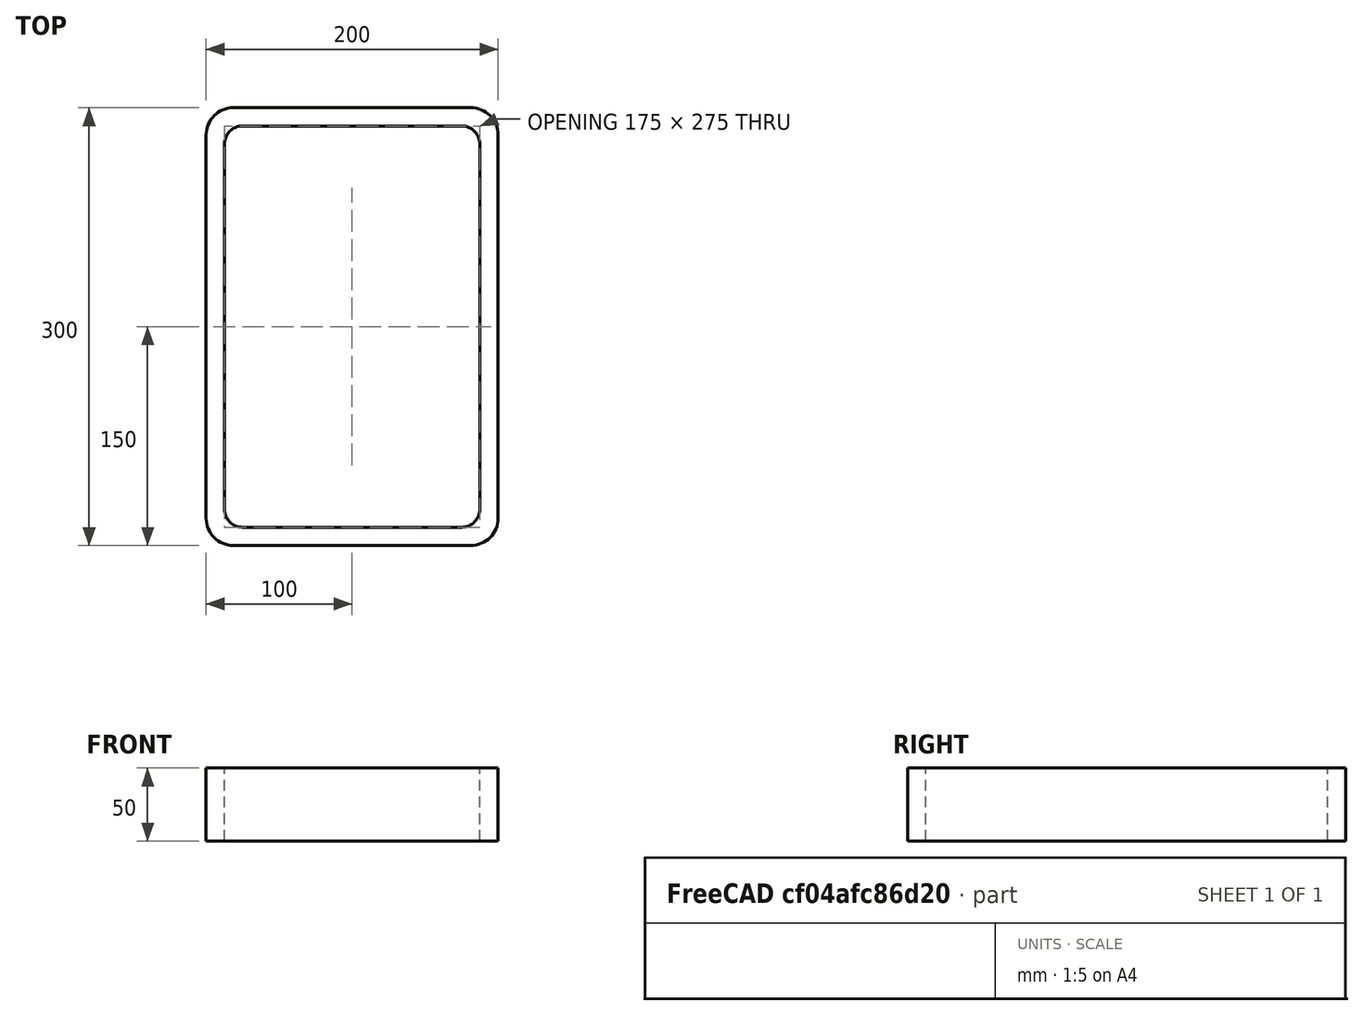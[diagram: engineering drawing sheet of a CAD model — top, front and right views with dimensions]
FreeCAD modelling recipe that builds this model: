
FCSTD DOCUMENT  (FreeCAD 0.15R4671 (Git))
Label: Rectangular hollow section 300x200x12.5 EN10219 S235JRH
License: All rights reserved
LicenseURL: http://en.wikipedia.org/wiki/All_rights_reserved
objects: Sketcher::SketchObject×1, Part::Extrusion×1
note: 2 computed .brp shape members not serialized (recipe doc carries the construction recipe); baked Part::Feature solids carry a one-line shape summary decoded from their .brp

FEATURE [Sketcher::SketchObject] Sketch
  sketch-geometry (16):
    g0: LineSegment StartX=-75 StartY=137.5 StartZ=0 EndX=75 EndY=137.5 EndZ=0
    g1: LineSegment StartX=87.5 StartY=125 StartZ=0 EndX=87.5 EndY=-125 EndZ=0
    g2: LineSegment StartX=75 StartY=-137.5 StartZ=0 EndX=-75 EndY=-137.5 EndZ=0
    g3: LineSegment StartX=-87.5 StartY=-125 StartZ=0 EndX=-87.5 EndY=125 EndZ=0
    g4: LineSegment StartX=-81.25 StartY=150 StartZ=0 EndX=81.25 EndY=150 EndZ=0
    g5: LineSegment StartX=100 StartY=131.25 StartZ=0 EndX=100 EndY=-131.25 EndZ=0
    g6: LineSegment StartX=81.25 StartY=-150 StartZ=0 EndX=-81.25 EndY=-150 EndZ=0
    g7: LineSegment StartX=-100 StartY=-131.25 StartZ=0 EndX=-100 EndY=131.25 EndZ=0
    g8: ArcOfCircle CenterX=-75 CenterY=125 CenterZ=0 NormalX=0 NormalY=0 NormalZ=1 Radius=12.5 StartAngle=1.5708 EndAngle=3.14159
    g9: ArcOfCircle CenterX=75 CenterY=125 CenterZ=0 NormalX=0 NormalY=0 NormalZ=1 Radius=12.5 StartAngle=0 EndAngle=1.5708
    g10: ArcOfCircle CenterX=75 CenterY=-125 CenterZ=0 NormalX=0 NormalY=0 NormalZ=1 Radius=12.5 StartAngle=4.71239 EndAngle=6.28319
    g11: ArcOfCircle CenterX=-75 CenterY=-125 CenterZ=0 NormalX=0 NormalY=0 NormalZ=1 Radius=12.5 StartAngle=3.14159 EndAngle=4.71239
    g12: ArcOfCircle CenterX=81.25 CenterY=131.25 CenterZ=0 NormalX=0 NormalY=0 NormalZ=1 Radius=18.75 StartAngle=0 EndAngle=1.5708
    g13: ArcOfCircle CenterX=81.25 CenterY=-131.25 CenterZ=0 NormalX=0 NormalY=0 NormalZ=1 Radius=18.75 StartAngle=4.71239 EndAngle=6.28319
    g14: ArcOfCircle CenterX=-81.25 CenterY=-131.25 CenterZ=0 NormalX=0 NormalY=0 NormalZ=1 Radius=18.75 StartAngle=3.14159 EndAngle=4.71239
    g15: ArcOfCircle CenterX=-81.25 CenterY=131.25 CenterZ=0 NormalX=0 NormalY=0 NormalZ=1 Radius=18.75 StartAngle=1.5708 EndAngle=3.14159
  constraints (36):
    c: Horizontal(g2)
    c: Vertical(g3)
    c: Horizontal(g6)
    c: Vertical(g7)
    c: Tangent(g3,g8) = 1.5708
    c: Tangent(g0,g8) = 1.5708
    c: Tangent(g0,g9) = 1.5708
    c: Tangent(g1,g9) = 1.5708
    c: Tangent(g1,g10) = 1.5708
    c: Tangent(g2,g10) = 1.5708
    c: Tangent(g2,g11) = 1.5708
    c: Tangent(g3,g11) = 1.5708
    c: Tangent(g4,g12) = 1.5708
    c: Tangent(g5,g12) = 1.5708
    c: Tangent(g5,g13) = 1.5708
    c: Tangent(g6,g13) = 1.5708
    c: Tangent(g6,g14) = 1.5708
    c: Tangent(g7,g14) = 1.5708
    c: Tangent(g7,g15) = 1.5708
    c: Tangent(g4,g15) = 1.5708
    c: Equal(g9,g8)
    c: Equal(g9,g11)
    c: Equal(g9,g10)
    c: Equal(g12,g15)
    c: Equal(g12,g14)
    c: Equal(g12,g13)
    c: Symmetric(g4,g6,g-1)
    c: Symmetric(g7,g5,g-2)
    c: DistanceY(g4,g6) = -300
    c: DistanceX(g7,g5) = 200
    c: Symmetric(g3,g1,g-2)
    c: Symmetric(g0,g2,g-1)
    c: DistanceY(g0,g4) = 12.5
    c: DistanceX(g5,g1) = -12.5
    c: Radius(g9) = 12.5
    c: Radius(g12) = 18.75
FEATURE [Part::Extrusion] Extrude  label="Rectangular hollow section 300x200x12.5 EN10219 S235JRH"
  Base = -> Sketch
  Dir = (0,0,50)
  Solid = true
